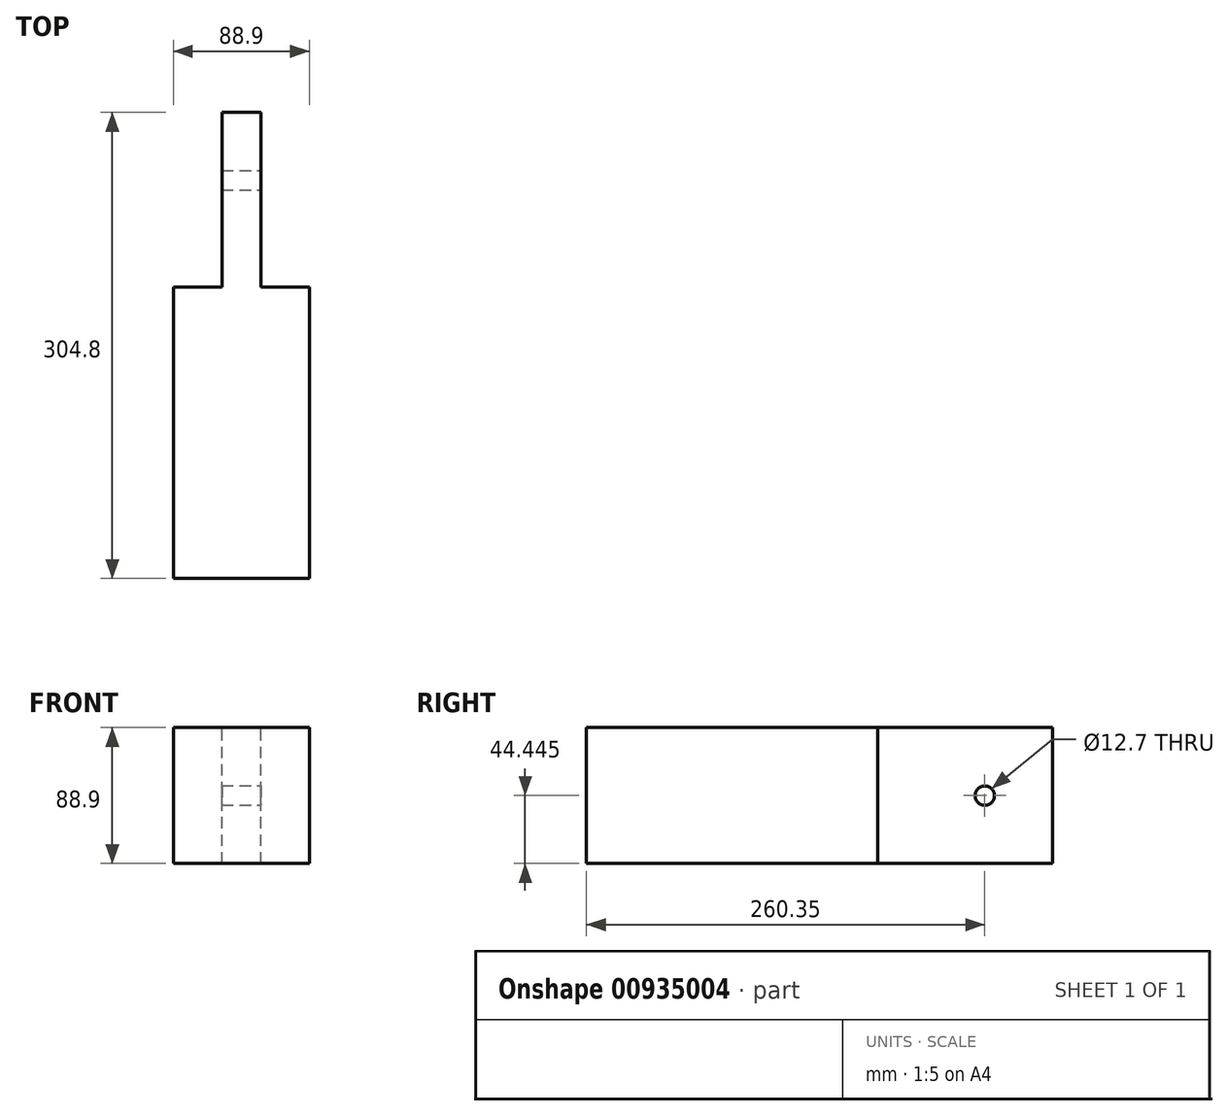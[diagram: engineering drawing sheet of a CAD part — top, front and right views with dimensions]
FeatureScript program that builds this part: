
annotation { "Feature Type Name" : "Feature", "Feature Type Description" : "" }
export const myFeature = defineFeature(function(context is Context, id is Id, definition is map)
    precondition{}
    {
        {
            var Q0;
            Q0=qCreatedBy(makeId("Front.planeOp"),FACE);
            var sketch = newSketch(context, id + "F0", { "sketchPlane" : qUnion([Q0])});
            skLineSegment(sketch, "E0.bottom", {"start": v(-42.71, 53.23) * mm, "end": v(46.19, 53.23) * mm});
            skLineSegment(sketch, "E0.top", {"start": v(-42.71, -35.67) * mm, "end": v(46.19, -35.67) * mm});
            skLineSegment(sketch, "E0.left", {"start": v(-42.71, 53.23) * mm, "end": v(-42.71, -35.67) * mm});
            skLineSegment(sketch, "E0.right", {"start": v(46.19, 53.23) * mm, "end": v(46.19, -35.67) * mm});
            skSolve(sketch);
        }
        {
            var Q0;
            Q0 = qSketchRegion(id + "F0", true);
            extrude(context, id + "F1", {"entities" : qUnion([Q0]), "depth" : 304.8 * mm, "offsetDistance" : 25.4 * mm});
        }
        {
            var Q0;
            Q0=qCreatedBy(makeId("Top.planeOp"),FACE);
            var sketch = newSketch(context, id + "F2", { "sketchPlane" : qUnion([Q0])});
            skLineSegment(sketch, "E1.bottom", {"start": v(-42.71, 0) * mm, "end": v(-10.96, 0) * mm});
            skLineSegment(sketch, "E1.top", {"start": v(-42.71, -114.3) * mm, "end": v(-10.96, -114.3) * mm});
            skLineSegment(sketch, "E1.left", {"start": v(-42.71, 0) * mm, "end": v(-42.71, -114.3) * mm});
            skLineSegment(sketch, "E1.right", {"start": v(-10.96, 0) * mm, "end": v(-10.96, -114.3) * mm});
            skPoint(sketch, "E2.oppositeSnap0", {"position": v(-26.84, -114.3) * mm});
            skLineSegment(sketch, "E2.bottom", {"start": v(46.19, 0) * mm, "end": v(14.44, 0) * mm});
            skLineSegment(sketch, "E2.top", {"start": v(46.19, -114.3) * mm, "end": v(14.44, -114.3) * mm});
            skLineSegment(sketch, "E2.left", {"start": v(46.19, 0) * mm, "end": v(46.19, -114.3) * mm});
            skLineSegment(sketch, "E2.right", {"start": v(14.44, 0) * mm, "end": v(14.44, -114.3) * mm});
            skSolve(sketch);
        }
        {
            var Q0;
            Q0 = qSketchRegion(id + "F2", true);
            extrude(context, id + "F3", {"entities" : qUnion([Q0]), "operationType" : NewBodyOperationType.REMOVE, "oppositeDirection" : true, "depth" : 254 * mm, "offsetDistance" : 25.4 * mm, "symmetric" : true});
        }
        {
            var Q0;
            Q0=makeQuery(id+"F3.boolean.opBoolean","COPY",FACE,{"derivedFrom":makeQuery(id+"F3.opExtrude","SWEPT_FACE",FACE,{"disambiguationData":[OSD([sQuery(id+"F2.wireOp",EDGE,"E2.right")])]})});
            var sketch = newSketch(context, id + "F4", { "sketchPlane" : qUnion([Q0])});
            skCircle(sketch, "E3", {"center": v(-44.45, 8.78) * mm, "radius": 6.35 * mm});
            skSolve(sketch);
        }
        {
            var Q0;
            Q0 = qSketchRegion(id + "F4", true);
            extrude(context, id + "F5", {"entities" : qUnion([Q0]), "operationType" : NewBodyOperationType.REMOVE, "oppositeDirection" : true, "depth" : 254 * mm, "offsetDistance" : 25.4 * mm, "symmetric" : true});
        }
    });
